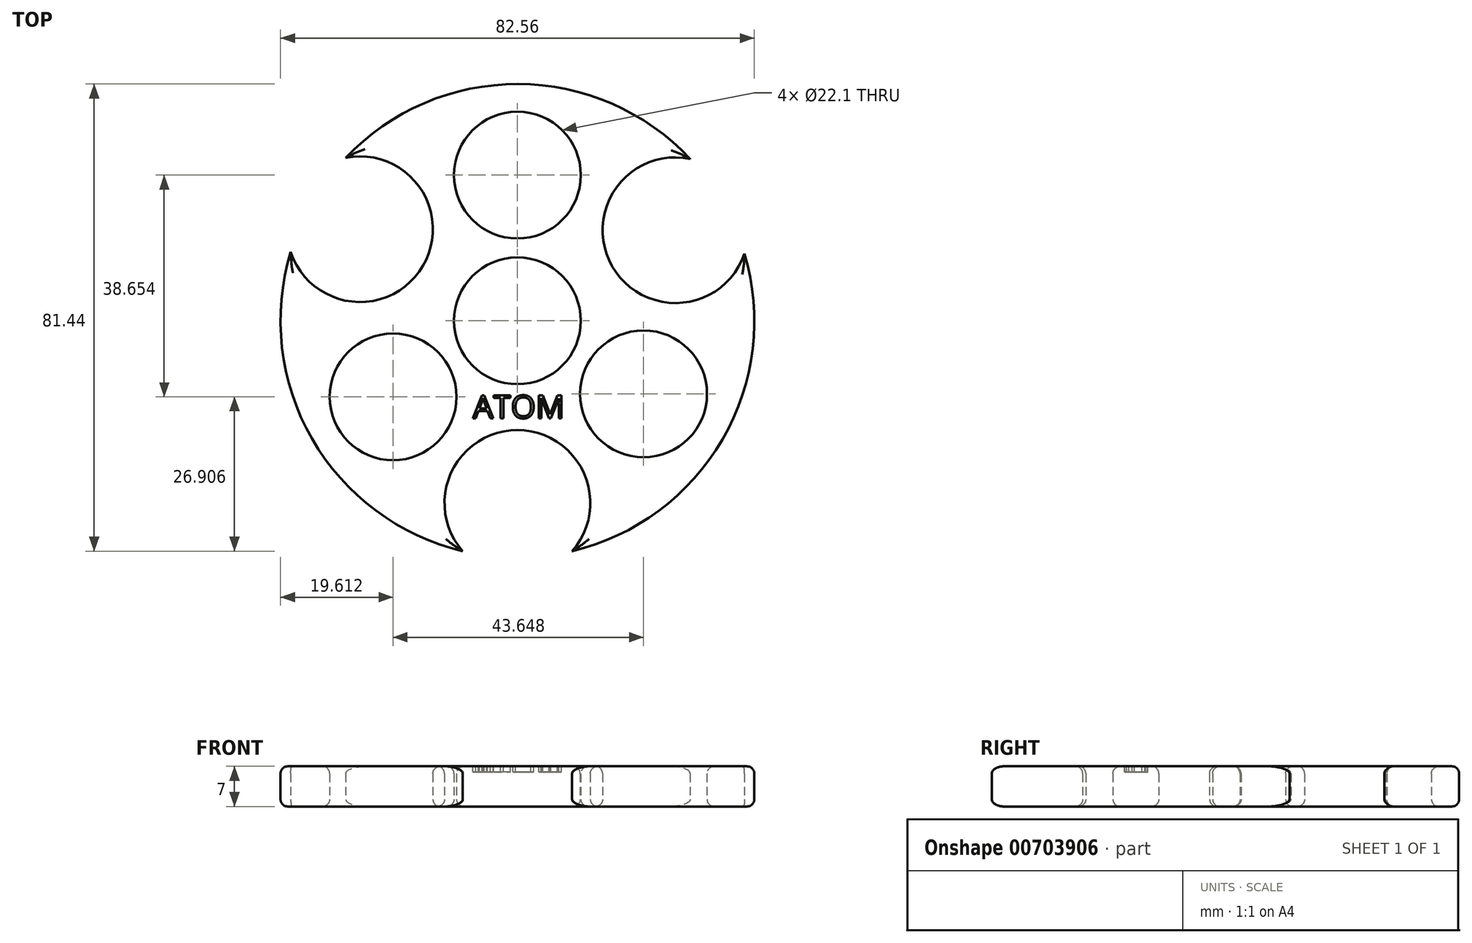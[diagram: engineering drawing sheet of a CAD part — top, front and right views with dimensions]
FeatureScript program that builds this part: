
annotation { "Feature Type Name" : "Feature", "Feature Type Description" : "" }
export const myFeature = defineFeature(function(context is Context, id is Id, definition is map)
    precondition{}
    {
        {
            var Q0;
            Q0=qCreatedBy(makeId("Top.planeOp"),FACE);
            var sketch = newSketch(context, id + "F0", { "sketchPlane" : qUnion([Q0])});
            skCircle(sketch, "E0", {"center": v(0, 0) * mm, "radius": 41.28 * mm});
            skCircle(sketch, "E1.cCircle", {"center": v(0, 0) * mm, "radius": 33.1 * mm, "construction": true});
            skLineSegment(sketch, "E1.0", {"start": v(28.69, -16.51) * mm, "end": v(-28.65, -16.59) * mm});
            skLineSegment(sketch, "E1.1", {"start": v(-28.65, -16.59) * mm, "end": v(-0.04, 33.1) * mm});
            skLineSegment(sketch, "E1.2", {"start": v(-0.04, 33.1) * mm, "end": v(28.69, -16.51) * mm});
            skSolve(sketch);
        }
        {
            var Q0;
            Q0=makeQuery(id+"F0.imprint","IMPRINT",FACE,{"disambiguationData":[TD([[makeQuery(id+"F0.imprint","IMPRINT",EDGE,{"derivedFrom":sQuery(id+"F0.wireOp",EDGE,"E0")}),1.0]])]});
            var sketch = newSketch(context, id + "F1", { "sketchPlane" : qUnion([Q0])});
            skCircle(sketch, "E2", {"center": v(0, 25.4) * mm, "radius": 11.05 * mm});
            skCircle(sketch, "E3", {"center": v(-21.67, -13.25) * mm, "radius": 11.05 * mm});
            skCircle(sketch, "E4", {"center": v(21.98, -12.73) * mm, "radius": 11.05 * mm});
            skCircle(sketch, "E5", {"center": v(0, 0) * mm, "radius": 11.05 * mm});
            skSolve(sketch);
        }
        {
            var Q0;
            Q0=makeQuery(id+"F0.imprint","IMPRINT",FACE,{"disambiguationData":[TD([[makeQuery(id+"F0.imprint","IMPRINT",EDGE,{"derivedFrom":sQuery(id+"F0.wireOp",EDGE,"E0")}),1.0]])]});
            var Q1;
            Q1=makeQuery(id+"F0.imprint","IMPRINT",FACE,{"disambiguationData":[TD([[makeQuery(id+"F0.imprint","IMPRINT",EDGE,{"derivedFrom":sQuery(id+"F0.wireOp",EDGE,"E1.0")}),-1.0]])]});
            extrude(context, id + "F2", {"entities" : qUnion([Q0, Q1]), "depth" : 7 * mm, "offsetDistance" : 25.4 * mm});
        }
        {
            var Q0;
            {var subQ0=sQuery(id+"F1.wireOp",EDGE,"E4");var subQ1=makeQuery(id+"F0.imprint","IMPRINT",EDGE,{"derivedFrom":sQuery(id+"F0.wireOp",EDGE,"E1.0")});var subQ2=makeQuery(id+"F1.imprint","INTERSECT",VERTEX,{"derivedFrom":[subQ1,subQ0]});Q0=makeQuery(id+"F1.imprint","IMPRINT",FACE,{"disambiguationData":[TD([[makeQuery(id+"F1.imprint","IMPRINT",EDGE,{"disambiguationData":[TD([[subQ2,1.0]])],"derivedFrom":subQ0}),1.0]])]});}
            var Q1;
            {var subQ0=sQuery(id+"F1.wireOp",EDGE,"E4");var subQ1=makeQuery(id+"F0.imprint","IMPRINT",EDGE,{"derivedFrom":sQuery(id+"F0.wireOp",EDGE,"E1.0")});var subQ2=makeQuery(id+"F1.imprint","INTERSECT",VERTEX,{"derivedFrom":[subQ1,subQ0]});Q1=makeQuery(id+"F1.imprint","IMPRINT",FACE,{"disambiguationData":[TD([[makeQuery(id+"F1.imprint","IMPRINT",EDGE,{"disambiguationData":[TD([[subQ2,-1.0]])],"derivedFrom":subQ0}),1.0]])]});}
            var Q2;
            Q2=makeQuery(id+"F1.imprint","IMPRINT",FACE,{"disambiguationData":[TD([[makeQuery(id+"F1.imprint","IMPRINT",EDGE,{"derivedFrom":sQuery(id+"F1.wireOp",EDGE,"E5")}),1.0]])]});
            var Q3;
            {var subQ0=sQuery(id+"F1.wireOp",EDGE,"E3");var subQ1=makeQuery(id+"F0.imprint","IMPRINT",EDGE,{"derivedFrom":sQuery(id+"F0.wireOp",EDGE,"E1.0")});var subQ2=makeQuery(id+"F1.imprint","INTERSECT",VERTEX,{"derivedFrom":[subQ1,subQ0]});Q3=makeQuery(id+"F1.imprint","IMPRINT",FACE,{"disambiguationData":[TD([[makeQuery(id+"F1.imprint","IMPRINT",EDGE,{"disambiguationData":[TD([[subQ2,1.0]])],"derivedFrom":subQ0}),1.0]])]});}
            var Q4;
            {var subQ0=sQuery(id+"F1.wireOp",EDGE,"E3");var subQ1=makeQuery(id+"F0.imprint","IMPRINT",EDGE,{"derivedFrom":sQuery(id+"F0.wireOp",EDGE,"E1.0")});var subQ2=makeQuery(id+"F1.imprint","INTERSECT",VERTEX,{"derivedFrom":[subQ1,subQ0]});Q4=makeQuery(id+"F1.imprint","IMPRINT",FACE,{"disambiguationData":[TD([[makeQuery(id+"F1.imprint","IMPRINT",EDGE,{"disambiguationData":[TD([[subQ2,-1.0]])],"derivedFrom":subQ0}),1.0]])]});}
            var Q5;
            {var subQ0=sQuery(id+"F1.wireOp",EDGE,"E2");var subQ1=makeQuery(id+"F0.imprint","IMPRINT",EDGE,{"derivedFrom":sQuery(id+"F0.wireOp",EDGE,"E1.1")});var subQ2=makeQuery(id+"F1.imprint","INTERSECT",VERTEX,{"derivedFrom":[subQ1,subQ0]});Q5=makeQuery(id+"F1.imprint","IMPRINT",FACE,{"disambiguationData":[TD([[makeQuery(id+"F1.imprint","IMPRINT",EDGE,{"disambiguationData":[TD([[subQ2,-1.0]])],"derivedFrom":subQ0}),1.0]])]});}
            var Q6;
            {var subQ0=sQuery(id+"F1.wireOp",EDGE,"E2");var subQ1=makeQuery(id+"F0.imprint","IMPRINT",EDGE,{"derivedFrom":sQuery(id+"F0.wireOp",EDGE,"E1.1")});var subQ2=makeQuery(id+"F1.imprint","INTERSECT",VERTEX,{"derivedFrom":[subQ1,subQ0]});Q6=makeQuery(id+"F1.imprint","IMPRINT",FACE,{"disambiguationData":[TD([[makeQuery(id+"F1.imprint","IMPRINT",EDGE,{"disambiguationData":[TD([[subQ2,1.0]])],"derivedFrom":subQ0}),1.0]])]});}
            var Q7;
            Q7=sQuery(id+"F1.wireOp",EDGE,"E2");
            var Q8;
            Q8=sQuery(id+"F1.wireOp",EDGE,"E5");
            var Q9;
            Q9=sQuery(id+"F1.wireOp",EDGE,"E3");
            var Q10;
            Q10=sQuery(id+"F1.wireOp",EDGE,"E4");
            extrude(context, id + "F3", {"entities" : qUnion([Q0, Q1, Q2, Q3, Q4, Q5, Q6]), "operationType" : NewBodyOperationType.REMOVE, "surfaceEntities" : qUnion([Q7, Q8, Q9, Q10]), "depth" : 7 * mm, "offsetDistance" : 25.4 * mm});
        }
        {
            var Q0;
            Q0=qCreatedBy(makeId("Top.planeOp"),FACE);
            var sketch = newSketch(context, id + "F4", { "sketchPlane" : qUnion([Q0])});
            skArc(sketch, "E6", {"start": v(-34, 5.1) * mm, "mid": v(-16.52, 9.5) * mm, "end": v(-21.03, 26.95) * mm});
            skArc(sketch, "E7", {"start": v(22.12, 27.29) * mm, "mid": v(16.35, 9.8) * mm, "end": v(34.11, 4.93) * mm});
            skArc(sketch, "E8", {"start": v(12.62, -33.18) * mm, "mid": v(0.76, -19.07) * mm, "end": v(-12.7, -31.67) * mm});
            skSolve(sketch);
        }
        {
            var Q0;
            Q0=sQuery(id+"F4.wireOp",VERTEX,"E6.center");
            var Q1;
            Q1=sQuery(id+"F4.wireOp",VERTEX,"E7.center");
            var Q2;
            Q2=sQuery(id+"F4.wireOp",VERTEX,"E8.center");
            var Q3;
            Q3=makeQuery(id+"F2.opExtrude","SWEPT_BODY",BODY,{"disambiguationData":[OSD([sQuery(id+"F0.wireOp",EDGE,"E0")])]});
            hole(context, id + "F5", {"style" : HoleStyle.SIMPLE, "endStyle" : HoleEndStyle.THROUGH, "oppositeDirection" : true, "holeDiameter" : 25.4 * mm, "majorDiameter" : 6.35 * mm, "isTappedThrough" : true, "tappedDepth" : 12.7 * mm, "tapClearance" : 3, "startFromSketch" : true, "locations" : qUnion([Q0, Q1, Q2]), "scope" : qUnion([Q3])});
        }
        {
            var Q0;
            Q0=makeQuery(id+"F2.opExtrude","CAP_FACE",FACE,{"disambiguationData":[OSD([sQuery(id+"F0.wireOp",EDGE,"E0")])],"isStart":false});
            fillet(context, id + "F6", {"entities" : qUnion([Q0]), "radius" : 1.27 * mm, "tangentPropagation" : true, "allowEdgeOverflow" : false});
        }
        {
            var Q0;
            Q0=makeQuery(id+"F2.opExtrude","CAP_FACE",FACE,{"disambiguationData":[OSD([sQuery(id+"F0.wireOp",EDGE,"E0")])],"isStart":true});
            fillet(context, id + "F7", {"entities" : qUnion([Q0]), "radius" : 1.27 * mm, "tangentPropagation" : true, "allowEdgeOverflow" : false});
        }
        {
            var Q0;
            Q0=makeQuery(id+"F2.opExtrude","CAP_FACE",FACE,{"disambiguationData":[OSD([sQuery(id+"F0.wireOp",EDGE,"E0")])],"isStart":false});
            var sketch = newSketch(context, id + "F8", { "sketchPlane" : qUnion([Q0])});
            skText(sketch, "E9", { "text": "ATOM", "fontName": "OpenSans-Regular.ttf"});
            const initialGuessF8  = {"E9": [-0.00774, -0.01698, 1, 0, 0.004]};
            skSetInitialGuess(sketch, initialGuessF8);
            skSolve(sketch);
        }
        {
            var Q0;
            Q0 = qSketchRegion(id + "F8", true);
            extrude(context, id + "F9", {"entities" : qUnion([Q0]), "operationType" : NewBodyOperationType.REMOVE, "oppositeDirection" : true, "depth" : 1 * mm, "offsetDistance" : 25 * mm});
        }
    });
